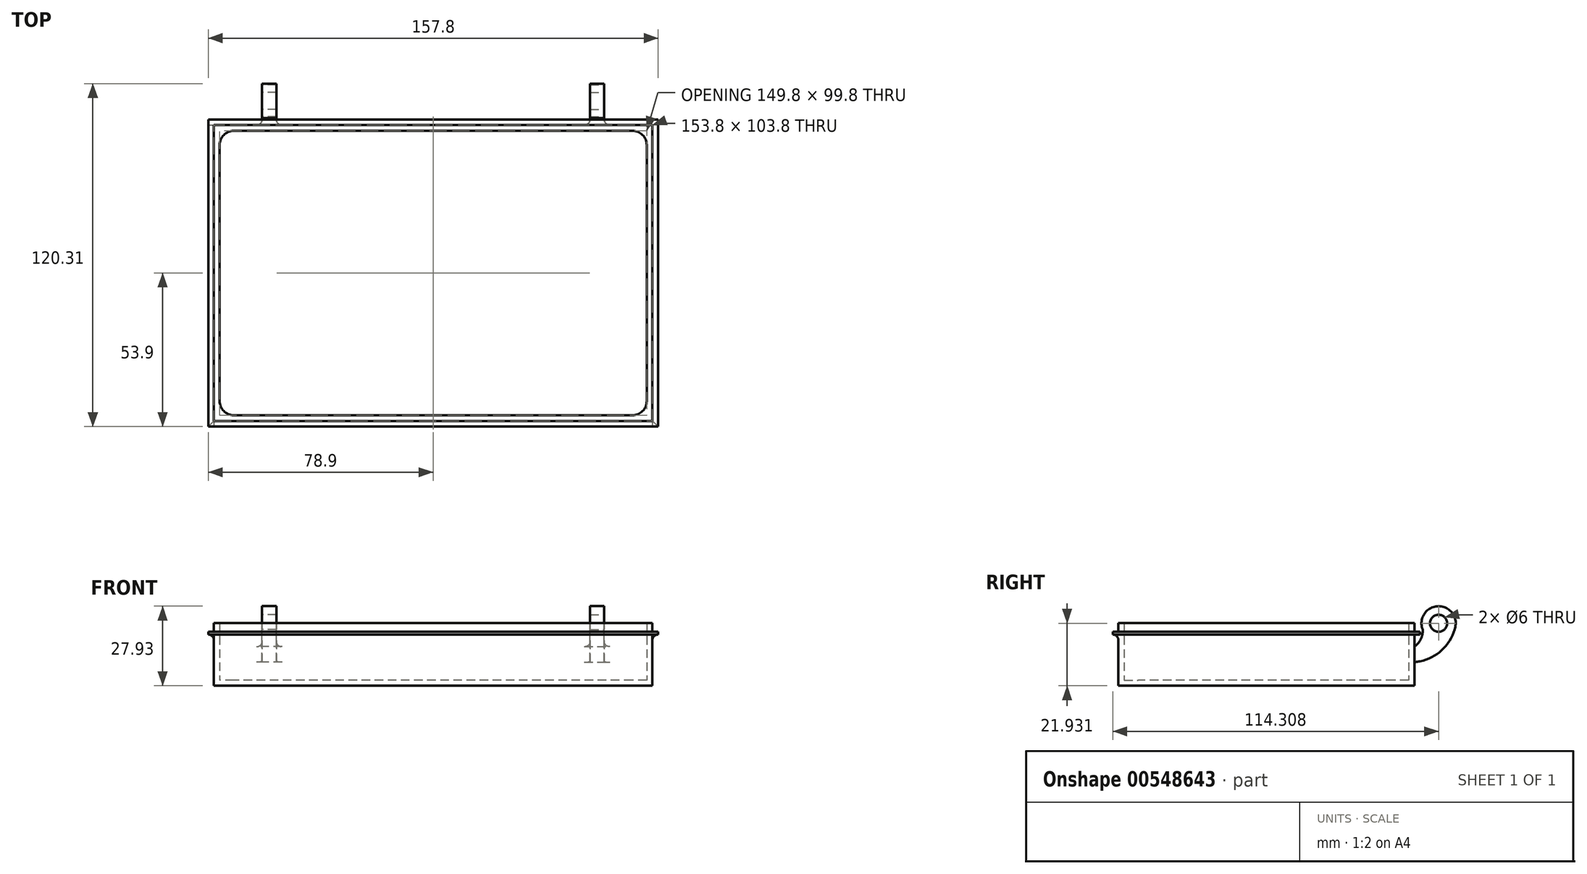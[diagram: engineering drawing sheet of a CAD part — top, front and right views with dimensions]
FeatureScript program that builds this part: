
annotation { "Feature Type Name" : "Feature", "Feature Type Description" : "" }
export const myFeature = defineFeature(function(context is Context, id is Id, definition is map)
    precondition{}
    {
        {
            var Q0;
            Q0=qCreatedBy(makeId("Top.planeOp"),FACE);
            var sketch = newSketch(context, id + "F0", { "sketchPlane" : qUnion([Q0])});
            skLineSegment(sketch, "E0.bottom", {"start": v(-74.9, 49.9) * mm, "end": v(74.9, 49.9) * mm});
            skLineSegment(sketch, "E0.top", {"start": v(-74.9, -49.9) * mm, "end": v(74.9, -49.9) * mm});
            skLineSegment(sketch, "E0.left", {"start": v(-74.9, 49.9) * mm, "end": v(-74.9, -49.9) * mm});
            skLineSegment(sketch, "E0.right", {"start": v(74.9, 49.9) * mm, "end": v(74.9, -49.9) * mm});
            skPoint(sketch, "E0.middle", {"position": v(0, 0) * mm});
            skSolve(sketch);
        }
        {
            var Q0;
            Q0=makeQuery(id+"F0.imprint","IMPRINT",FACE,{"disambiguationData":[TD([[makeQuery(id+"F0.imprint","IMPRINT",EDGE,{"derivedFrom":sQuery(id+"F0.wireOp",EDGE,"E0.bottom")}),-1.0]])]});
            extrude(context, id + "F1", {"entities" : qUnion([Q0]), "depth" : 20 * mm, "offsetDistance" : 25 * mm});
        }
        {
            var Q0;
            Q0=makeQuery(id+"F1.opExtrude","CAP_FACE",FACE,{"disambiguationData":[OSD([sQuery(id+"F0.wireOp",EDGE,"E0.bottom"),sQuery(id+"F0.wireOp",EDGE,"E0.top"),sQuery(id+"F0.wireOp",EDGE,"E0.left"),sQuery(id+"F0.wireOp",EDGE,"E0.right")])],"isStart":false});
            shell(context, id + "F2", {"entities" : qUnion([Q0]), "thickness" : 2 * mm, "oppositeDirection" : true});
        }
        {
            var Q0;
            Q0=makeQuery(id+"F1.opExtrude","SWEPT_FACE",FACE,{"disambiguationData":[OSD([sQuery(id+"F0.wireOp",EDGE,"E0.top")])]});
            var sketch = newSketch(context, id + "F3", { "sketchPlane" : qUnion([Q0])});
            skLineSegment(sketch, "E1", {"start": v(-76.9, 17) * mm, "end": v(76.9, 17) * mm});
            skLineSegment(sketch, "E2", {"start": v(-76.9, 16) * mm, "end": v(76.9, 16) * mm});
            skSolve(sketch);
        }
        {
            var Q0;
            {var subQ0=sQuery(id+"F3.wireOp",EDGE,"E1");Q0=makeQuery(id+"F3.imprint","IMPRINT",FACE,{"disambiguationData":[TD([[makeQuery(id+"F3.imprint","IMPRINT",EDGE,{"derivedFrom":subQ0}),-1.0]])]});}
            extrude(context, id + "F4", {"entities" : qUnion([Q0]), "operationType" : NewBodyOperationType.ADD, "depth" : 2 * mm, "offsetDistance" : 25 * mm});
        }
        {
            var Q0;
            Q0=makeQuery(id+"F1.opExtrude","SWEPT_FACE",FACE,{"disambiguationData":[OSD([sQuery(id+"F0.wireOp",EDGE,"E0.bottom")])]});
            var sketch = newSketch(context, id + "F5", { "sketchPlane" : qUnion([Q0])});
            skLineSegment(sketch, "E3", {"start": v(-76.9, 17) * mm, "end": v(76.9, 17) * mm});
            skLineSegment(sketch, "E4", {"start": v(-76.9, 16) * mm, "end": v(76.9, 16) * mm});
            skSolve(sketch);
        }
        {
            var Q0;
            {var subQ0=sQuery(id+"F5.wireOp",EDGE,"E3");Q0=makeQuery(id+"F5.imprint","IMPRINT",FACE,{"disambiguationData":[TD([[makeQuery(id+"F5.imprint","IMPRINT",EDGE,{"derivedFrom":subQ0}),-1.0]])]});}
            extrude(context, id + "F6", {"entities" : qUnion([Q0]), "operationType" : NewBodyOperationType.ADD, "depth" : 2 * mm, "offsetDistance" : 25 * mm});
        }
        {
            var Q0;
            {var subQ0=sQuery(id+"F0.wireOp",EDGE,"E0.left");Q0=makeQuery(id+"F6.boolean.opBoolean","MERGE",FACE,{"derivedFrom":[makeQuery(id+"F4.boolean.opBoolean","MERGE",FACE,{"derivedFrom":[makeQuery(id+"F1.opExtrude","SWEPT_FACE",FACE,{"disambiguationData":[OSD([subQ0])]}),makeQuery(id+"F4.opExtrude","SWEPT_FACE",FACE,{"disambiguationData":[OSD([sQuery(id+"F0.wireOp",EDGE,"E0.top"),subQ0])]})]}),makeQuery(id+"F6.opExtrude","SWEPT_FACE",FACE,{"disambiguationData":[OSD([sQuery(id+"F0.wireOp",EDGE,"E0.bottom"),subQ0])]})]});}
            var sketch = newSketch(context, id + "F7", { "sketchPlane" : qUnion([Q0])});
            skLineSegment(sketch, "E5", {"start": v(-53.9, 17) * mm, "end": v(53.9, 17) * mm});
            skLineSegment(sketch, "E6", {"start": v(-53.9, 16) * mm, "end": v(53.9, 16) * mm});
            skSolve(sketch);
        }
        {
            var Q0;
            {var subQ1=sQuery(id+"F0.wireOp",EDGE,"E0.left");var subQ3=sQuery(id+"F0.wireOp",EDGE,"E0.top");var subQ19=makeQuery(id+"F4.opExtrude","CAP_EDGE",EDGE,{"disambiguationData":[OSD([subQ3,subQ1])],"isStart":false});Q0=makeQuery(id+"F7.imprint","IMPRINT",FACE,{"disambiguationData":[TD([[makeQuery(id+"F7.imprint","IMPRINT",EDGE,{"derivedFrom":subQ19}),-1.0]])]});}
            extrude(context, id + "F8", {"entities" : qUnion([Q0]), "operationType" : NewBodyOperationType.ADD, "depth" : 2 * mm, "offsetDistance" : 25 * mm});
        }
        {
            var Q0;
            {var subQ0=sQuery(id+"F0.wireOp",EDGE,"E0.right");Q0=makeQuery(id+"F6.boolean.opBoolean","MERGE",FACE,{"derivedFrom":[makeQuery(id+"F4.boolean.opBoolean","MERGE",FACE,{"derivedFrom":[makeQuery(id+"F1.opExtrude","SWEPT_FACE",FACE,{"disambiguationData":[OSD([subQ0])]}),makeQuery(id+"F4.opExtrude","SWEPT_FACE",FACE,{"disambiguationData":[OSD([sQuery(id+"F0.wireOp",EDGE,"E0.top"),subQ0])]})]}),makeQuery(id+"F6.opExtrude","SWEPT_FACE",FACE,{"disambiguationData":[OSD([sQuery(id+"F0.wireOp",EDGE,"E0.bottom"),subQ0])]})]});}
            var sketch = newSketch(context, id + "F9", { "sketchPlane" : qUnion([Q0])});
            skLineSegment(sketch, "E7", {"start": v(-53.9, 17) * mm, "end": v(53.9, 17) * mm});
            skLineSegment(sketch, "E8", {"start": v(-53.9, 16) * mm, "end": v(53.9, 16) * mm});
            skSolve(sketch);
        }
        {
            var Q0;
            {var subQ1=sQuery(id+"F0.wireOp",EDGE,"E0.right");var subQ3=sQuery(id+"F0.wireOp",EDGE,"E0.top");var subQ16=makeQuery(id+"F4.opExtrude","CAP_EDGE",EDGE,{"disambiguationData":[OSD([subQ3,subQ1])],"isStart":false});Q0=makeQuery(id+"F9.imprint","IMPRINT",FACE,{"disambiguationData":[TD([[makeQuery(id+"F9.imprint","IMPRINT",EDGE,{"derivedFrom":subQ16}),1.0]])]});}
            extrude(context, id + "F10", {"entities" : qUnion([Q0]), "operationType" : NewBodyOperationType.ADD, "depth" : 2 * mm, "offsetDistance" : 25 * mm});
        }
        {
            var Q0;
            Q0=makeQuery(id+"F10.opExtrude","CAP_EDGE",EDGE,{"disambiguationData":[OSD([sQuery(id+"F9.wireOp",EDGE,"E8")])],"isStart":true});
            var Q1;
            Q1=makeQuery(id+"F6.opExtrude","CAP_EDGE",EDGE,{"disambiguationData":[OSD([sQuery(id+"F5.wireOp",EDGE,"E4")])],"isStart":true});
            var Q2;
            Q2=makeQuery(id+"F8.opExtrude","CAP_EDGE",EDGE,{"disambiguationData":[OSD([sQuery(id+"F7.wireOp",EDGE,"E6")])],"isStart":true});
            var Q3;
            Q3=makeQuery(id+"F4.opExtrude","CAP_EDGE",EDGE,{"disambiguationData":[OSD([sQuery(id+"F3.wireOp",EDGE,"E2")])],"isStart":true});
            fillet(context, id + "F11", {"entities" : qUnion([Q0, Q1, Q2, Q3]), "radius" : 2 * mm, "tangentPropagation" : true, "allowEdgeOverflow" : false});
        }
        {
            var Q0;
            Q0=makeQuery(id+"F2.opShell","OFFSET_EDGE",EDGE,{"disambiguationData":[OSD([sQuery(id+"F0.wireOp",EDGE,"E0.top"),sQuery(id+"F0.wireOp",EDGE,"E0.right")])]});
            var Q1;
            Q1=makeQuery(id+"F2.opShell","OFFSET_EDGE",EDGE,{"disambiguationData":[OSD([sQuery(id+"F0.wireOp",EDGE,"E0.top"),sQuery(id+"F0.wireOp",EDGE,"E0.left")])]});
            var Q2;
            Q2=makeQuery(id+"F2.opShell","OFFSET_EDGE",EDGE,{"disambiguationData":[OSD([sQuery(id+"F0.wireOp",EDGE,"E0.bottom"),sQuery(id+"F0.wireOp",EDGE,"E0.left")])]});
            var Q3;
            Q3=makeQuery(id+"F2.opShell","OFFSET_EDGE",EDGE,{"disambiguationData":[OSD([sQuery(id+"F0.wireOp",EDGE,"E0.bottom"),sQuery(id+"F0.wireOp",EDGE,"E0.right")])]});
            fillet(context, id + "F12", {"entities" : qUnion([Q0, Q1, Q2, Q3]), "radius" : 5 * mm, "tangentPropagation" : true, "allowEdgeOverflow" : false});
        }
        {
            var Q0;
            Q0=qCreatedBy(makeId("Right.planeOp"),FACE);
            var sketch = newSketch(context, id + "F13", { "sketchPlane" : qUnion([Q0])});
            skCircle(sketch, "E9", {"center": v(59.9, 19.9) * mm, "radius": 6 * mm});
            skCircle(sketch, "E10", {"center": v(59.9, 19.9) * mm, "radius": 3 * mm});
            skLineSegment(sketch, "E11", {"start": v(51.99, 17) * mm, "end": v(69.58, 17) * mm, "construction": true});
            skLineSegment(sketch, "E12", {"start": v(53, 17) * mm, "end": v(53, 26.01) * mm, "construction": true});
            skLineSegment(sketch, "E13", {"start": v(51.91, 6.38) * mm, "end": v(51.8, 6.27) * mm});
            skLineSegment(sketch, "E14", {"start": v(51.8, 6.27) * mm, "end": v(51.91, 6.27) * mm});
            skLineSegment(sketch, "E15", {"start": v(65.89, 19.53) * mm, "end": v(65.86, 20.58) * mm});
            skLineSegment(sketch, "E16", {"start": v(51.91, 11.65) * mm, "end": v(51.91, 6.27) * mm});
            skPoint(sketch, "E17.orphan", {"position": v(53.92, 8.3) * mm});
            skArc(sketch, "E18", {"start": v(51.91, 6.27) * mm, "mid": v(61.9, 10.48) * mm, "end": v(65.86, 20.58) * mm});
            skPoint(sketch, "E19.orphan", {"position": v(53.92, 14.33) * mm});
            skPoint(sketch, "E20.start.orphan", {"position": v(53.92, 20.37) * mm});
            skArc(sketch, "E21", {"start": v(51.91, 11.65) * mm, "mid": v(53.76, 14.27) * mm, "end": v(54.44, 17.4) * mm});
            skSolve(sketch);
        }
        {
            var Q0;
            Q0=qCreatedBy(makeId("Right.planeOp"),FACE);
            cPlane(context, id + "F14", {"entities" : qUnion([Q0]), "cplaneType" : CPlaneType.OFFSET, "offset" : 60 * mm, "width" : 150 * mm, "height" : 150 * mm});
        }
        {
            var Q0;
            Q0=qCreatedBy(id+"F14.planeOp",FACE);
            var sketch = newSketch(context, id + "F15", { "sketchPlane" : qUnion([Q0])});
            skCircle(sketch, "E22", {"center": v(60.4, 19.93) * mm, "radius": 6 * mm});
            skCircle(sketch, "E23", {"center": v(60.4, 19.93) * mm, "radius": 3 * mm});
            skLineSegment(sketch, "E24", {"start": v(51.82, 11.69) * mm, "end": v(51.82, 6.31) * mm});
            skArc(sketch, "E25", {"start": v(51.82, 11.69) * mm, "mid": v(54.14, 14.32) * mm, "end": v(54.81, 17.77) * mm});
            skArc(sketch, "E26", {"start": v(51.82, 6.31) * mm, "mid": v(60.7, 9.8) * mm, "end": v(66, 17.73) * mm});
            skSolve(sketch);
        }
        {
            var Q0;
            Q0=makeQuery(id+"F15.imprint","IMPRINT",FACE,{"disambiguationData":[TD([[makeQuery(id+"F15.imprint","IMPRINT",EDGE,{"derivedFrom":sQuery(id+"F15.wireOp",EDGE,"E23")}),-1.0]])]});
            var Q1;
            {var subQ4=sQuery(id+"F15.wireOp",EDGE,"E24");Q1=makeQuery(id+"F15.imprint","IMPRINT",FACE,{"disambiguationData":[TD([[makeQuery(id+"F15.imprint","IMPRINT",EDGE,{"derivedFrom":subQ4}),1.0]])]});}
            extrude(context, id + "F16", {"entities" : qUnion([Q0, Q1]), "operationType" : NewBodyOperationType.ADD, "oppositeDirection" : true, "depth" : 5 * mm, "offsetDistance" : 25 * mm});
        }
        {
            var Q0;
            {var subQ3=sQuery(id+"F0.wireOp",EDGE,"E0.bottom");Q0=makeQuery(id+"F16.boolean.opBoolean","INTERSECT",EDGE,{"derivedFrom":[makeQuery(id+"F6.boolean.opBoolean","SPLIT",FACE,{"disambiguationData":[TD([makeQuery(id+"F6.opExtrude","SWEPT_FACE",FACE,{"disambiguationData":[OSD([sQuery(id+"F5.wireOp",EDGE,"E4")])]})])],"derivedFrom":makeQuery(id+"F1.opExtrude","SWEPT_FACE",FACE,{"disambiguationData":[OSD([subQ3])]})}),makeQuery(id+"F16.opExtrude","CAP_FACE",FACE,{"disambiguationData":[OSD([sQuery(id+"F15.wireOp",EDGE,"E22"),sQuery(id+"F15.wireOp",EDGE,"E23"),sQuery(id+"F15.wireOp",EDGE,"E24"),sQuery(id+"F15.wireOp",EDGE,"c05ac9b5-523e-4178-8347-921d6ccc0e00"),sQuery(id+"F15.wireOp",EDGE,"56b891a8-1283-4a23-8f40-525a9a4dccd0")])],"isStart":true})]});}
            var Q1;
            {var subQ3=sQuery(id+"F0.wireOp",EDGE,"E0.bottom");Q1=makeQuery(id+"F16.boolean.opBoolean","INTERSECT",EDGE,{"derivedFrom":[makeQuery(id+"F6.boolean.opBoolean","SPLIT",FACE,{"disambiguationData":[TD([makeQuery(id+"F6.opExtrude","SWEPT_FACE",FACE,{"disambiguationData":[OSD([sQuery(id+"F5.wireOp",EDGE,"E4")])]})])],"derivedFrom":makeQuery(id+"F1.opExtrude","SWEPT_FACE",FACE,{"disambiguationData":[OSD([subQ3])]})}),makeQuery(id+"F16.opExtrude","SWEPT_FACE",FACE,{"disambiguationData":[OSD([sQuery(id+"F15.wireOp",EDGE,"c05ac9b5-523e-4178-8347-921d6ccc0e00")])]})]});}
            var Q2;
            {var subQ3=sQuery(id+"F0.wireOp",EDGE,"E0.bottom");Q2=makeQuery(id+"F16.boolean.opBoolean","INTERSECT",EDGE,{"derivedFrom":[makeQuery(id+"F6.boolean.opBoolean","SPLIT",FACE,{"disambiguationData":[TD([makeQuery(id+"F6.opExtrude","SWEPT_FACE",FACE,{"disambiguationData":[OSD([sQuery(id+"F5.wireOp",EDGE,"E4")])]})])],"derivedFrom":makeQuery(id+"F1.opExtrude","SWEPT_FACE",FACE,{"disambiguationData":[OSD([subQ3])]})}),makeQuery(id+"F16.opExtrude","CAP_FACE",FACE,{"disambiguationData":[OSD([sQuery(id+"F15.wireOp",EDGE,"E22"),sQuery(id+"F15.wireOp",EDGE,"E23"),sQuery(id+"F15.wireOp",EDGE,"E24"),sQuery(id+"F15.wireOp",EDGE,"c05ac9b5-523e-4178-8347-921d6ccc0e00"),sQuery(id+"F15.wireOp",EDGE,"56b891a8-1283-4a23-8f40-525a9a4dccd0")])],"isStart":false})]});}
            fillet(context, id + "F17", {"entities" : qUnion([Q0, Q1, Q2]), "radius" : 2 * mm, "tangentPropagation" : true, "allowEdgeOverflow" : false});
        }
        {
            var Q0;
            Q0=makeQuery(id+"F1.opExtrude","SWEPT_BODY",BODY,{"disambiguationData":[OSD([sQuery(id+"F0.wireOp",EDGE,"E0.bottom"),sQuery(id+"F0.wireOp",EDGE,"E0.top"),sQuery(id+"F0.wireOp",EDGE,"E0.left"),sQuery(id+"F0.wireOp",EDGE,"E0.right")])]});
            var Q1;
            Q1=qCreatedBy(makeId("Right.planeOp"),FACE);
            mirror(context, id + "F18", {"entities" : qUnion([Q0]), "mirrorPlane" : qUnion([Q1])});
        }
    });
